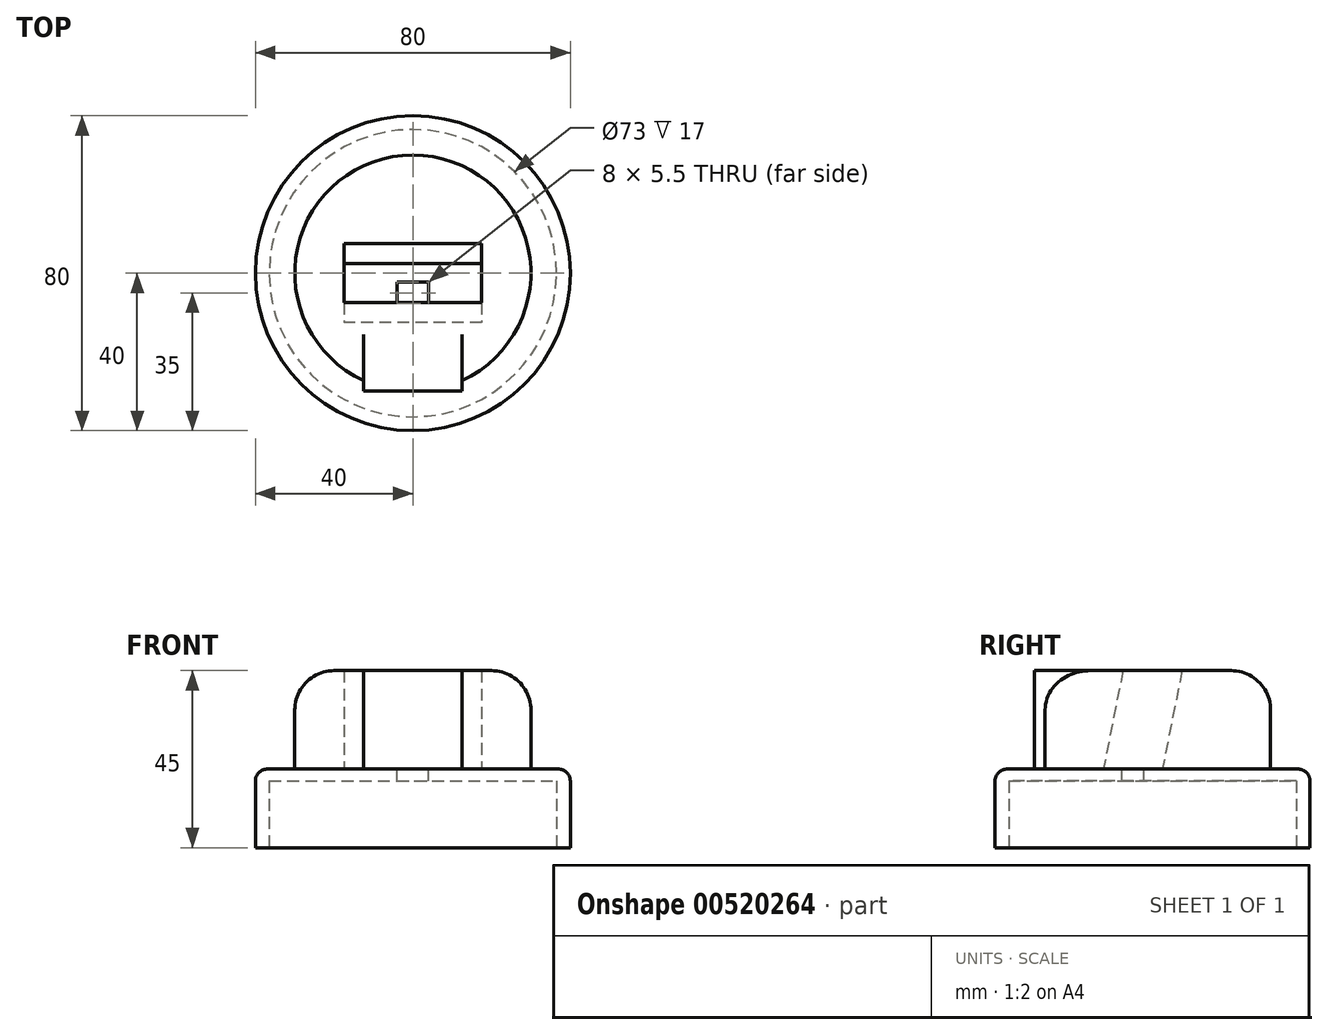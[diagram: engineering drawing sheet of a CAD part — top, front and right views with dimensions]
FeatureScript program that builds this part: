
annotation { "Feature Type Name" : "Feature", "Feature Type Description" : "" }
export const myFeature = defineFeature(function(context is Context, id is Id, definition is map)
    precondition{}
    {
        {
            var Q0;
            Q0=qCreatedBy(makeId("Front.planeOp"),FACE);
            var sketch = newSketch(context, id + "F0", { "sketchPlane" : qUnion([Q0])});
            skLineSegment(sketch, "E0", {"start": v(0, 0) * mm, "end": v(-40, 0) * mm});
            skLineSegment(sketch, "E1", {"start": v(-40, 0) * mm, "end": v(-40, 20) * mm});
            skLineSegment(sketch, "E2", {"start": v(-40, 20) * mm, "end": v(-30, 20) * mm});
            skLineSegment(sketch, "E3", {"start": v(0, 20) * mm, "end": v(0, 0) * mm});
            skLineSegment(sketch, "E4", {"start": v(-30, 20) * mm, "end": v(-30, 45) * mm});
            skLineSegment(sketch, "E5", {"start": v(-30, 45) * mm, "end": v(0, 45) * mm});
            skLineSegment(sketch, "E6", {"start": v(0, 45) * mm, "end": v(0, 20) * mm});
            skSolve(sketch);
        }
        {
            var Q0;
            Q0=makeQuery(id+"F0.imprint","IMPRINT",FACE,{"disambiguationData":[TD([[makeQuery(id+"F0.imprint","IMPRINT",EDGE,{"derivedFrom":sQuery(id+"F0.wireOp",EDGE,"E0")}),-1.0]])]});
            var Q1;
            Q1=sQuery(id+"F0.wireOp",EDGE,"E6");
            revolve(context, id + "F1", {"entities" : qUnion([Q0]), "axis" : qUnion([Q1]), "revolveType" : RevolveType.FULL});
        }
        {
            var Q0;
            Q0=qCreatedBy(makeId("Front.planeOp"),FACE);
            cPlane(context, id + "F2", {"entities" : qUnion([Q0]), "cplaneType" : CPlaneType.OFFSET, "offset" : 30 * mm, "width" : 150 * mm, "height" : 150 * mm});
        }
        {
            var Q0;
            Q0=qCreatedBy(id+"F2.planeOp",FACE);
            var sketch = newSketch(context, id + "F3", { "sketchPlane" : qUnion([Q0])});
            skLineSegment(sketch, "E7.bottom", {"start": v(12.5, 45) * mm, "end": v(-12.5, 45) * mm});
            skLineSegment(sketch, "E7.top", {"start": v(12.5, 20) * mm, "end": v(-12.5, 20) * mm});
            skLineSegment(sketch, "E7.left", {"start": v(12.5, 45) * mm, "end": v(12.5, 20) * mm});
            skLineSegment(sketch, "E7.right", {"start": v(-12.5, 45) * mm, "end": v(-12.5, 20) * mm});
            skPoint(sketch, "E7.middle", {"position": v(0, 32.5) * mm});
            skSolve(sketch);
        }
        {
            var Q0;
            Q0=makeQuery(id+"F3.imprint","IMPRINT",FACE,{"disambiguationData":[TD([[makeQuery(id+"F3.imprint","IMPRINT",EDGE,{"derivedFrom":sQuery(id+"F3.wireOp",EDGE,"E7.bottom")}),1.0]])]});
            extrude(context, id + "F4", {"entities" : qUnion([Q0]), "operationType" : NewBodyOperationType.ADD, "oppositeDirection" : true, "depth" : 25 * mm, "offsetDistance" : 25 * mm});
        }
        {
            var Q0;
            Q0=makeQuery(id+"F1.opRevolve","SWEPT_EDGE",EDGE,{"disambiguationData":[OSD([sQuery(id+"F0.wireOp",EDGE,"E4"),sQuery(id+"F0.wireOp",EDGE,"E5")])]});
            fillet(context, id + "F5", {"entities" : qUnion([Q0]), "radius" : 10 * mm, "tangentPropagation" : true, "allowEdgeOverflow" : false});
        }
        {
            var Q0;
            Q0=makeQuery(id+"F1.opRevolve","SWEPT_EDGE",EDGE,{"disambiguationData":[OSD([sQuery(id+"F0.wireOp",EDGE,"E1"),sQuery(id+"F0.wireOp",EDGE,"E2")])]});
            fillet(context, id + "F6", {"entities" : qUnion([Q0]), "radius" : 3 * mm, "tangentPropagation" : true, "allowEdgeOverflow" : false});
        }
        {
            var Q0;
            Q0=makeQuery(id+"F4.boolean.opBoolean","MERGE",FACE,{"derivedFrom":[makeQuery(id+"F1.opRevolve","SWEPT_FACE",FACE,{"disambiguationData":[OSD([sQuery(id+"F0.wireOp",EDGE,"E5")])]}),makeQuery(id+"F4.opExtrude","SWEPT_FACE",FACE,{"disambiguationData":[OSD([sQuery(id+"F3.wireOp",EDGE,"E7.bottom")])]})]});
            var sketch = newSketch(context, id + "F7", { "sketchPlane" : qUnion([Q0])});
            skLineSegment(sketch, "E8.bottom", {"start": v(17.5, 7.5) * mm, "end": v(-17.5, 7.5) * mm});
            skLineSegment(sketch, "E8.top", {"start": v(17.5, -7.5) * mm, "end": v(-17.5, -7.5) * mm});
            skLineSegment(sketch, "E8.left", {"start": v(17.5, 7.5) * mm, "end": v(17.5, -7.5) * mm});
            skLineSegment(sketch, "E8.right", {"start": v(-17.5, 7.5) * mm, "end": v(-17.5, -7.5) * mm});
            skPoint(sketch, "E8.middle", {"position": v(0, 0) * mm});
            skSolve(sketch);
        }
        {
            var Q0;
            Q0=makeQuery(id+"F1.opRevolve","SWEPT_FACE",FACE,{"disambiguationData":[OSD([sQuery(id+"F0.wireOp",EDGE,"E2")])]});
            var sketch = newSketch(context, id + "F8", { "sketchPlane" : qUnion([Q0])});
            skLineSegment(sketch, "E9.bottom", {"start": v(17.5, 2.5) * mm, "end": v(-17.5, 2.5) * mm});
            skLineSegment(sketch, "E9.top", {"start": v(17.5, -12.5) * mm, "end": v(-17.5, -12.5) * mm});
            skLineSegment(sketch, "E9.left", {"start": v(17.5, 2.5) * mm, "end": v(17.5, -12.5) * mm});
            skLineSegment(sketch, "E9.right", {"start": v(-17.5, 2.5) * mm, "end": v(-17.5, -12.5) * mm});
            skPoint(sketch, "E9.middle", {"position": v(0, -5) * mm});
            skSolve(sketch);
        }
        {
            var Q1;
            Q1=makeQuery(id+"F7.imprint","IMPRINT",FACE,{"disambiguationData":[TD([[makeQuery(id+"F7.imprint","IMPRINT",EDGE,{"derivedFrom":sQuery(id+"F7.wireOp",EDGE,"E8.bottom")}),1.0]])]});
            var Q2;
            Q2 = qSketchRegion(id + "F8", true);
            loft(context, id + "F9", {"operationType" : NewBodyOperationType.REMOVE, "sheetProfilesArray" : [{ "sheetProfileEntities" : qUnion([Q1]) }, { "sheetProfileEntities" : qUnion([Q2]) }]});
        }
        {
            var Q0;
            Q0=makeQuery(id+"F1.opRevolve","SWEPT_FACE",FACE,{"disambiguationData":[OSD([sQuery(id+"F0.wireOp",EDGE,"E0")])]});
            var sketch = newSketch(context, id + "F10", { "sketchPlane" : qUnion([Q0])});
            skCircle(sketch, "E10.0", {"center": v(0, 0) * mm, "radius": 36.5 * mm});
            skSolve(sketch);
        }
        {
            var Q0;
            Q0=makeQuery(id+"F10.imprint","IMPRINT",FACE,{"disambiguationData":[TD([[makeQuery(id+"F10.imprint","IMPRINT",EDGE,{"derivedFrom":sQuery(id+"F10.wireOp",EDGE,"E10.0")}),1.0]])]});
            extrude(context, id + "F11", {"entities" : qUnion([Q0]), "operationType" : NewBodyOperationType.REMOVE, "oppositeDirection" : true, "depth" : 17 * mm, "offsetDistance" : 25 * mm});
        }
        {
            var Q0;
            Q0=makeQuery(id+"F9.boolean.opBoolean","COPY",FACE,{"derivedFrom":makeQuery(id+"F9.opLoft","CAP_FACE",FACE,{"disambiguationData":[OSD([makeQuery(id+"F8.imprint","IMPRINT",FACE,{"disambiguationData":[TD([[makeQuery(id+"F8.imprint","IMPRINT",EDGE,{"derivedFrom":sQuery(id+"F8.wireOp",EDGE,"E9.bottom")}),1.0]])]})])],"isStart":true})});
            var sketch = newSketch(context, id + "F12", { "sketchPlane" : qUnion([Q0])});
            skLineSegment(sketch, "E11.bottom", {"start": v(4, -2.25) * mm, "end": v(-4, -2.25) * mm});
            skLineSegment(sketch, "E11.top", {"start": v(4, -7.75) * mm, "end": v(-4, -7.75) * mm});
            skLineSegment(sketch, "E11.left", {"start": v(4, -2.25) * mm, "end": v(4, -7.75) * mm});
            skLineSegment(sketch, "E11.right", {"start": v(-4, -2.25) * mm, "end": v(-4, -7.75) * mm});
            skPoint(sketch, "E11.middle", {"position": v(0, -5) * mm});
            skSolve(sketch);
        }
        {
            var Q0;
            Q0=makeQuery(id+"F12.imprint","IMPRINT",FACE,{"disambiguationData":[TD([[makeQuery(id+"F12.imprint","IMPRINT",EDGE,{"derivedFrom":sQuery(id+"F12.wireOp",EDGE,"E11.bottom")}),1.0]])]});
            extrude(context, id + "F13", {"entities" : qUnion([Q0]), "operationType" : NewBodyOperationType.REMOVE, "endBound" : BoundingType.THROUGH_ALL, "oppositeDirection" : true, "depth" : 25 * mm, "offsetDistance" : 25 * mm});
        }
    });
